# Revit family: Żaluzja ścienna tłumiąca ZSR-T
name_source: partatom
category: Terminale wentylacyjne
revit_build: Autodesk Revit 2018 (Build: 20190510_1515(x64)
units: mm (PartAtom-declared; Revit-internal decimal feet)

## family parameters
Numer OmniClass = 23.75.70.21.27.11
Oparty na płaszczyźnie roboczej = Nie
Punkt obliczania pomieszczeń = Nie
Tnij formami wycięć po wczytaniu = Nie
Typ części = Normalny
Tytuł OmniClass = Diffusers, Registers, and Grilles
Współdzielony = Nie
Wymiar okrągłego złącza = Użyj średnicy
Zawsze pionowo = Tak

## types (3) — shared parameters
Atest Higieniczny = HK/K/0522/02/2016
Deklaracja zgodności = 9/DZ/2020/K
IfcExportAs = IfcFlowTerminal
Karta katalogowa = https://www.sawpol.pl
Komentarze do typu = Żaluzja ścienna tłumiąca
Maksymalna szerokość otworu montażowego modułu = 2500 mm  [stored 8.2021 ft]
Maksymalna wysokość otworu montażowego modułu = 1800 mm  [stored 5.90551 ft]
Minimalna szerokość otworu montażowego = 300 mm
Minimalna wysokość otworu montażowego = 500 mm  [stored 1.64042 ft]
Model = ZSR-T
Obraz typu = ZSR.png
Producent = PPHU SAW-POL
URL = https://www.sawpol.pl
Wymiary - informacja = Jeżeli żaluzja przekracza maksymalne wymiary modułu (2500x1800) konieczne jest dzielenie produktu na moduły, których wymiary są ustalane indywidualnie

## per-type parameters (varying)
| type | H | L | Materiał | Materiał piór | Szerokość otworu montażowego | Szerokość wlotu | Wykonanie aluminium | Wykonanie stal nierdzewna | Wykonanie stal ocynkowana | Wysokość otworu montażowego | Wysokość wlotu |
| OC | 1000 mm  [stored 3.28084 ft] | 1000 mm  [stored 3.28084 ft] | SAW_POL Stal ocynkowana | SAW_POL Stal ocynkowana | 1000 mm  [stored 3.28084 ft] | 990 mm  [stored 3.24803 ft] | Nie | Nie | Tak | 1000 mm  [stored 3.28084 ft] | 990 mm  [stored 3.24803 ft] |
| AL | 2500 mm  [stored 8.2021 ft] | 2000 mm  [stored 6.56168 ft] | SAW_POL Aluminium | SAW_POL Aluminium | 2000 mm  [stored 6.56168 ft] | 1990 mm  [stored 6.52887 ft] | Tak | Nie | Nie | 2000 mm  [stored 6.56168 ft] | 2490 mm |
| KO | 1000 mm  [stored 3.28084 ft] | 1000 mm  [stored 3.28084 ft] | SAW-POL Stal nierdzewna | SAW-POL Stal nierdzewna | 1000 mm  [stored 3.28084 ft] | 990 mm  [stored 3.24803 ft] | Nie | Tak | Nie | 1000 mm  [stored 3.28084 ft] | 990 mm  [stored 3.24803 ft] |

note: [stored X ft] marks values corroborated as IEEE doubles in the binary element streams (Revit-internal decimal feet)
